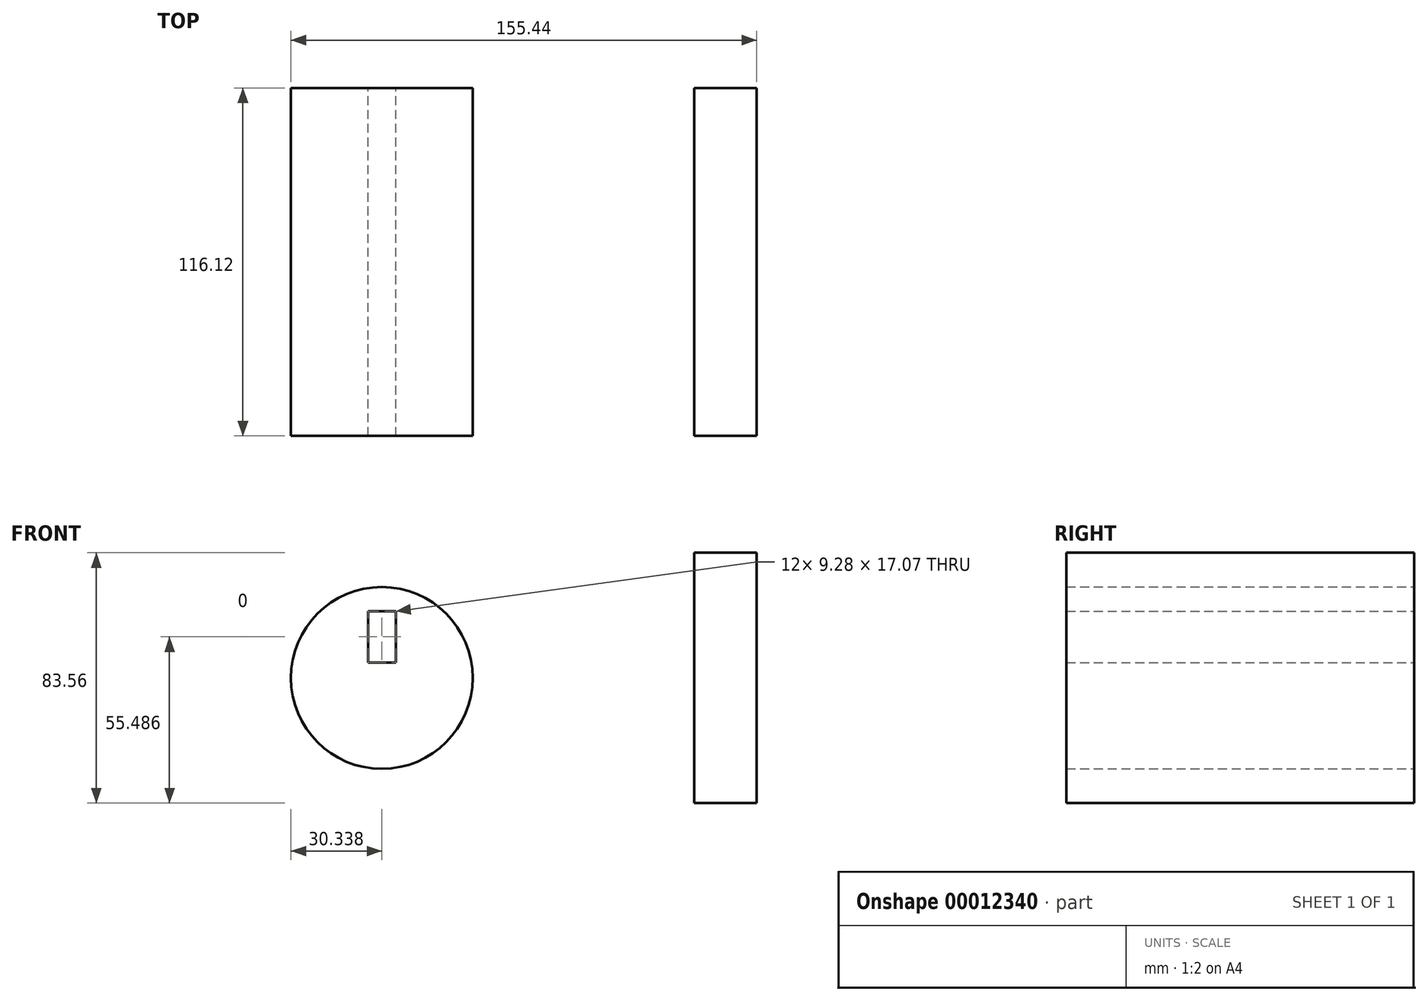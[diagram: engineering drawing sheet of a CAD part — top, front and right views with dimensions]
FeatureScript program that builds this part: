
annotation { "Feature Type Name" : "Feature", "Feature Type Description" : "" }
export const myFeature = defineFeature(function(context is Context, id is Id, definition is map)
    precondition{}
    {
        {
            var Q0;
            Q0=qCreatedBy(makeId("Front.planeOp"),FACE);
            var sketch = newSketch(context, id + "F0", { "sketchPlane" : qUnion([Q0])});
            skCircle(sketch, "E0", {"center": v(-87.23, 0) * mm, "radius": 30.34 * mm});
            skLineSegment(sketch, "E1.rect.bottom", {"start": v(-82.59, 22.24) * mm, "end": v(-91.87, 22.24) * mm});
            skLineSegment(sketch, "E1.rect.top", {"start": v(-82.59, 5.17) * mm, "end": v(-91.87, 5.17) * mm});
            skLineSegment(sketch, "E1.rect.left", {"start": v(-82.59, 22.24) * mm, "end": v(-82.59, 5.17) * mm});
            skLineSegment(sketch, "E1.rect.right", {"start": v(-91.87, 22.24) * mm, "end": v(-91.87, 5.17) * mm});
            skPoint(sketch, "E1.rect.middle", {"position": v(-87.23, 13.7) * mm});
            skLineSegment(sketch, "E2.rect.bottom", {"start": v(37.87, 41.78) * mm, "end": v(16.98, 41.78) * mm});
            skLineSegment(sketch, "E2.rect.top", {"start": v(37.87, -41.78) * mm, "end": v(16.98, -41.78) * mm});
            skLineSegment(sketch, "E2.rect.left", {"start": v(37.87, 41.78) * mm, "end": v(37.87, -41.78) * mm});
            skLineSegment(sketch, "E2.rect.right", {"start": v(16.98, 41.78) * mm, "end": v(16.98, -41.78) * mm});
            skPoint(sketch, "E2.rect.middle", {"position": v(27.43, 0) * mm});
            skSolve(sketch);
        }
        {
            var Q0;
            Q0 = qSketchRegion(id + "F0", true);
            extrude(context, id + "F1", {"entities" : qUnion([Q0]), "endBound" : BoundingType.SYMMETRIC, "depth" : 116.13 * mm});
        }
        {
            var Q0;
            Q0=qCreatedBy(makeId("Front.planeOp"),FACE);
            var sketch = newSketch(context, id + "F2", { "sketchPlane" : qUnion([Q0])});
            skLineSegment(sketch, "E3", {"start": v(-87.23, 0) * mm, "end": v(-63.04, -18.31) * mm});
            skSolve(sketch);
        }
    });
